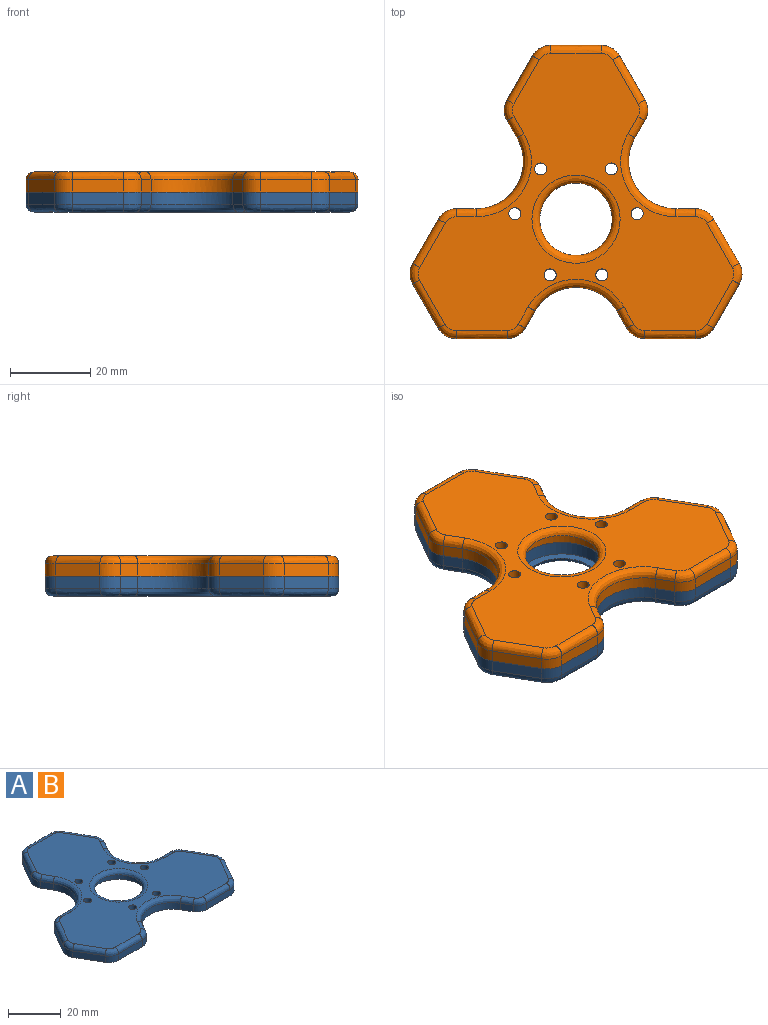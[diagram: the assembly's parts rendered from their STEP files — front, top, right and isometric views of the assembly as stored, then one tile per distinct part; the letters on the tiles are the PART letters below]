
ASSEMBLY  parts=2 mates=1
PART A: 92 faces, bbox 83.4x73.2x5 mm
  f0: plane 82.9x73.18mm, normal (0,0,-1), area 1699mm2, adj f1,f2,f3,f4,f5,f6,f7,f8
  f1: cylinder r=11.81mm len=20.45mm, axis (0,0,-1), area 74.2mm2, adj f0,f2,f34,f58
  f2: plane 4.29x3mm, normal (-0.87,-0.5,0), area 14.9mm2, adj f0,f1,f3,f56
  f3: cylinder r=5.2mm len=4.5mm, axis (0,0,-1), area 16.3mm2, adj f0,f2,f4,f54
  f4: plane 12.7x3mm, normal (0,-1,0), area 38.1mm2, adj f0,f3,f5,f52
  f5: cylinder r=5.2mm len=4.5mm, axis (0,0,-1), area 16.3mm2, adj f0,f4,f6,f50
  f6: plane 11x6.35mm, normal (0.87,-0.5,0), area 38.1mm2, adj f0,f5,f7,f48
  f7: cylinder r=5.2mm len=5.2mm, axis (0,0,-1), area 16.3mm2, adj f0,f6,f8,f46
  f8: plane 11x6.35mm, normal (0.87,0.5,0), area 38.1mm2, adj f0,f7,f9,f44
  f9: cylinder r=5.2mm len=4.5mm, axis (0,0,-1), area 16.3mm2, adj f0,f8,f10,f42
  f10: plane 4.96x3mm, normal (0,1,0), area 14.9mm2, adj f0,f9,f11,f40
  f11: cylinder r=11.81mm len=17.71mm, axis (0,0,-1), area 74.2mm2, adj f0,f10,f12,f38
  f12: plane 4.29x3mm, normal (0.87,-0.5,0), area 14.9mm2, adj f0,f11,f13,f39
  f13: cylinder r=5.2mm len=5.2mm, axis (0,0,-1), area 16.3mm2, adj f0,f12,f14,f41
  f14: plane 11x6.35mm, normal (0.87,0.5,0), area 38.1mm2, adj f0,f13,f15,f43
  f15: cylinder r=5.2mm len=4.5mm, axis (0,0,-1), area 16.3mm2, adj f0,f14,f16,f45
  f16: plane 12.7x3mm, normal (0,1,0), area 38.1mm2, adj f0,f15,f17,f47
  f17: cylinder r=5.2mm len=4.5mm, axis (0,0,-1), area 16.3mm2, adj f0,f16,f18,f49
  f18: plane 11x6.35mm, normal (-0.87,0.5,0), area 38.1mm2, adj f0,f17,f19,f51
  f19: cylinder r=5.2mm len=5.2mm, axis (0,0,-1), area 16.3mm2, adj f0,f18,f20,f53
  f20: plane 4.29x3mm, normal (-0.87,-0.5,0), area 14.9mm2, adj f0,f19,f21,f55
  f21: cylinder r=11.81mm len=17.71mm, axis (0,0,-1), area 74.2mm2, adj f0,f20,f22,f57
  f22: plane 4.96x3mm, normal (0,1,0), area 14.9mm2, adj f0,f21,f23,f59
  f23: cylinder r=5.2mm len=4.5mm, axis (0,0,-1), area 16.3mm2, adj f0,f22,f24,f61
  f24: plane 11x6.35mm, normal (-0.87,0.5,0), area 38.1mm2, adj f0,f23,f25,f63
  f25: cylinder r=5.2mm len=5.2mm, axis (0,0,-1), area 16.3mm2, adj f0,f24,f26,f65
  f26: plane 11x6.35mm, normal (-0.87,-0.5,0), area 38.1mm2, adj f0,f25,f27,f67
  f27: cylinder r=5.2mm len=4.5mm, axis (0,0,-1), area 16.3mm2, adj f0,f26,f28,f66
  f28: plane 12.7x3mm, normal (0,-1,0), area 38.1mm2, adj f0,f27,f29,f64
  f29: cylinder r=5.2mm len=4.5mm, axis (0,0,-1), area 16.3mm2, adj f0,f28,f34,f62
  f30: cylinder r=1.5mm len=5mm, axis (0,0,-1), area 47.1mm2, adj f0,f37
  f31: cylinder r=1.5mm len=5mm, axis (0,0,-1), area 47.1mm2, adj f0,f37
  f32: cylinder r=1.5mm len=5mm, axis (0,0,-1), area 47.1mm2, adj f0,f37
  f33: cylinder r=1.5mm len=5mm, axis (0,0,-1), area 47.1mm2, adj f0,f37
  f34: plane 4.29x3mm, normal (0.87,-0.5,0), area 14.9mm2, adj f0,f1,f29,f60
  f35: cylinder r=1.5mm len=5mm, axis (0,0,-1), area 47.1mm2, adj f0,f37
  f36: cylinder r=1.5mm len=5mm, axis (0,0,-1), area 47.1mm2, adj f0,f37
  f37: plane 78.91x69.2mm, normal (0,0,1), area 2401.6mm2, adj f30,f31,f32,f33,f35,f36,f38,f39
  f38: bspline ~20.71x13.81mm, area 84.9mm2, adj f11,f37,f39,f40
  f39: bspline ~5.29x4.21mm, area 16.1mm2, adj f12,f37,f38,f41
  f40: bspline ~4.96x2mm, area 16.1mm2, adj f10,f37,f38,f42
  f41: bspline ~5.2x2.65mm, area 15.3mm2, adj f13,f37,f39,f43
  f42: bspline ~4.5x3.6mm, area 15.3mm2, adj f9,f37,f40,f44
  f43: bspline ~12x8.08mm, area 41.2mm2, adj f14,f37,f41,f45
  f44: bspline ~12x8.08mm, area 41.2mm2, adj f8,f37,f42,f46
  f45: bspline ~4.5x3.6mm, area 15.3mm2, adj f15,f37,f43,f47
  f46: bspline ~5.2x2.65mm, area 15.3mm2, adj f7,f37,f44,f48
  f47: bspline ~12.7x2mm, area 41.2mm2, adj f16,f37,f45,f49
  f48: bspline ~12x8.08mm, area 41.2mm2, adj f6,f37,f46,f50
  f49: bspline ~4.5x3.6mm, area 15.3mm2, adj f17,f37,f47,f51
  f50: bspline ~4.5x3.6mm, area 15.3mm2, adj f5,f37,f48,f52
  f51: bspline ~12x8.08mm, area 41.2mm2, adj f18,f37,f49,f53
  f52: bspline ~12.7x2mm, area 41.2mm2, adj f4,f37,f50,f54
  f53: bspline ~5.2x2.65mm, area 15.3mm2, adj f19,f37,f51,f55
  f54: bspline ~4.5x3.6mm, area 15.3mm2, adj f3,f37,f52,f56
  f55: bspline ~5.29x4.21mm, area 16.1mm2, adj f20,f37,f53,f57
  f56: bspline ~5.29x4.21mm, area 16.1mm2, adj f2,f37,f54,f58
  f57: bspline ~20.71x13.81mm, area 84.9mm2, adj f21,f37,f55,f59
  f58: bspline ~23.91x7.9mm, area 84.9mm2, adj f1,f37,f56,f60
  f59: bspline ~4.96x2mm, area 16.1mm2, adj f22,f37,f57,f61
  f60: bspline ~5.29x4.21mm, area 16.1mm2, adj f34,f37,f58,f62
  f61: bspline ~4.5x3.6mm, area 15.3mm2, adj f23,f37,f59,f63
  f62: bspline ~4.5x3.6mm, area 15.3mm2, adj f29,f37,f60,f64
  f63: bspline ~12x8.08mm, area 41.2mm2, adj f24,f37,f61,f65
  f64: bspline ~12.7x2mm, area 41.2mm2, adj f28,f37,f62,f66
  f65: bspline ~5.2x2.65mm, area 15.3mm2, adj f25,f37,f63,f67
  f66: bspline ~4.5x3.6mm, area 15.3mm2, adj f27,f37,f64,f67
  f67: bspline ~12x8.08mm, area 41.2mm2, adj f26,f37,f65,f66
  f68: bspline ~22x22mm, area 169.1mm2, adj f37,f70
  f69: cylinder r=11mm len=22mm, axis (0,0,-1), area 241.9mm2, adj f0,f70
  f70: plane 22.02x22.02mm, normal (0,0,-1), area 123.6mm2, adj f68,f69
  f71: plane 12.7x3.5mm, normal (0,-1,0), area 44.4mm2, adj f0,f72,f76,f77
  f72: plane 11x6.35mm, normal (0.87,-0.5,0), area 44.5mm2, adj f0,f71,f73,f77
  f73: plane 11x6.35mm, normal (0.87,0.5,0), area 44.4mm2, adj f0,f72,f74,f77
  f74: plane 12.7x3.5mm, normal (0,1,0), area 44.4mm2, adj f0,f73,f75,f77
  f75: plane 11x6.35mm, normal (-0.87,0.5,0), area 44.4mm2, adj f0,f74,f76,f77
  f76: plane 11x6.35mm, normal (-0.87,-0.5,0), area 44.5mm2, adj f0,f71,f75,f77
  f77: plane 25.4x22mm, normal (0,0,-1), area 419mm2, adj f71,f72,f73,f74,f75,f76
  f78: plane 11x6.35mm, normal (-0.87,0.5,0), area 44.5mm2, adj f0,f79,f83,f84
  f79: plane 11x6.35mm, normal (-0.87,-0.5,0), area 44.5mm2, adj f0,f78,f80,f84
  f80: plane 12.7x3.5mm, normal (0,-1,0), area 44.4mm2, adj f0,f79,f81,f84
  f81: plane 11x6.35mm, normal (0.87,-0.5,0), area 44.5mm2, adj f0,f80,f82,f84
  f82: plane 11x6.35mm, normal (0.87,0.5,0), area 44.5mm2, adj f0,f81,f83,f84
  f83: plane 12.7x3.5mm, normal (0,1,0), area 44.4mm2, adj f0,f78,f82,f84
  f84: plane 25.4x22mm, normal (0,0,-1), area 419mm2, adj f78,f79,f80,f81,f82,f83
  f85: plane 11x6.35mm, normal (-0.87,0.5,0), area 44.4mm2, adj f0,f86,f90,f91
  f86: plane 11x6.35mm, normal (-0.87,-0.5,0), area 44.5mm2, adj f0,f85,f87,f91
  f87: plane 12.7x3.5mm, normal (0,-1,0), area 44.4mm2, adj f0,f86,f88,f91
  f88: plane 11x6.35mm, normal (0.87,-0.5,0), area 44.5mm2, adj f0,f87,f89,f91
  f89: plane 11x6.35mm, normal (0.87,0.5,0), area 44.4mm2, adj f0,f88,f90,f91
  f90: plane 12.7x3.5mm, normal (0,1,0), area 44.4mm2, adj f0,f85,f89,f91
  f91: plane 25.4x22mm, normal (0,0,-1), area 419mm2, adj f85,f86,f87,f88,f89,f90
PART B: same geometry as A
PLACE A rot(axis=(0,1,0),180deg) t=(0,0,0)mm
PLACE B at identity
MATE fastened A.f69 <-> B.f69  axis (0,0,-1) through (0,0,0)mm
